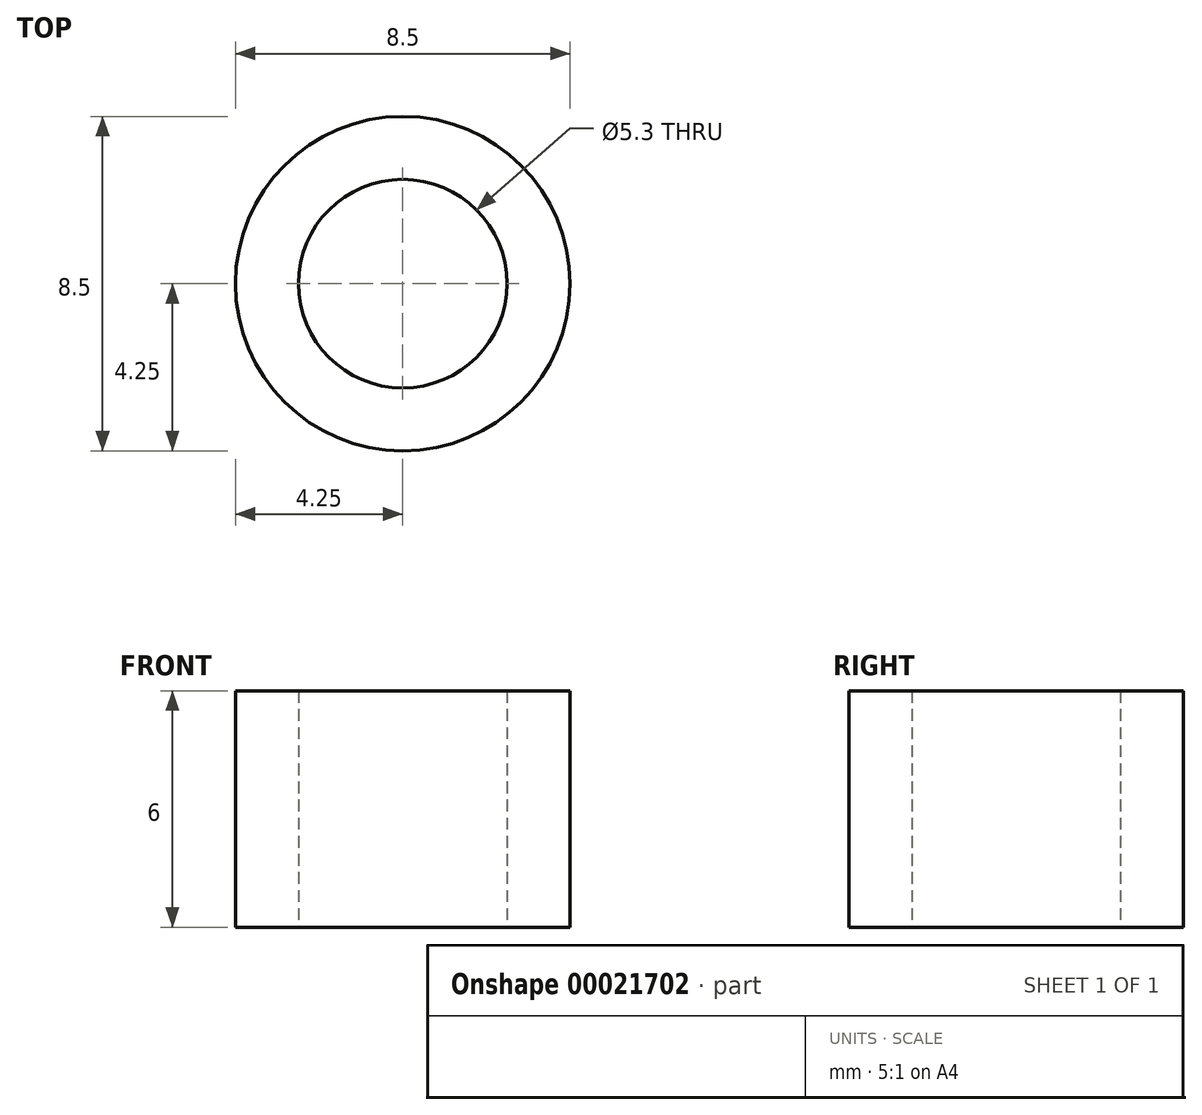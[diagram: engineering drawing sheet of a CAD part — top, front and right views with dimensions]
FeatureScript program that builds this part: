
annotation { "Feature Type Name" : "Feature", "Feature Type Description" : "" }
export const myFeature = defineFeature(function(context is Context, id is Id, definition is map)
    precondition{}
    {
        {
            var Q0;
            Q0=qCreatedBy(makeId("Top.planeOp"),FACE);
            var sketch = newSketch(context, id + "F0", { "sketchPlane" : qUnion([Q0])});
            skCircle(sketch, "E0", {"center": v(0, 0) * mm, "radius": 2.65 * mm});
            skCircle(sketch, "E1", {"center": v(0, 0) * mm, "radius": 4.25 * mm});
            skSolve(sketch);
        }
        {
            var Q0;
            Q0 = qSketchRegion(id + "F0", true);
            extrude(context, id + "F1", {"entities" : qUnion([Q0]), "depth" : 6 * mm});
        }
    });
